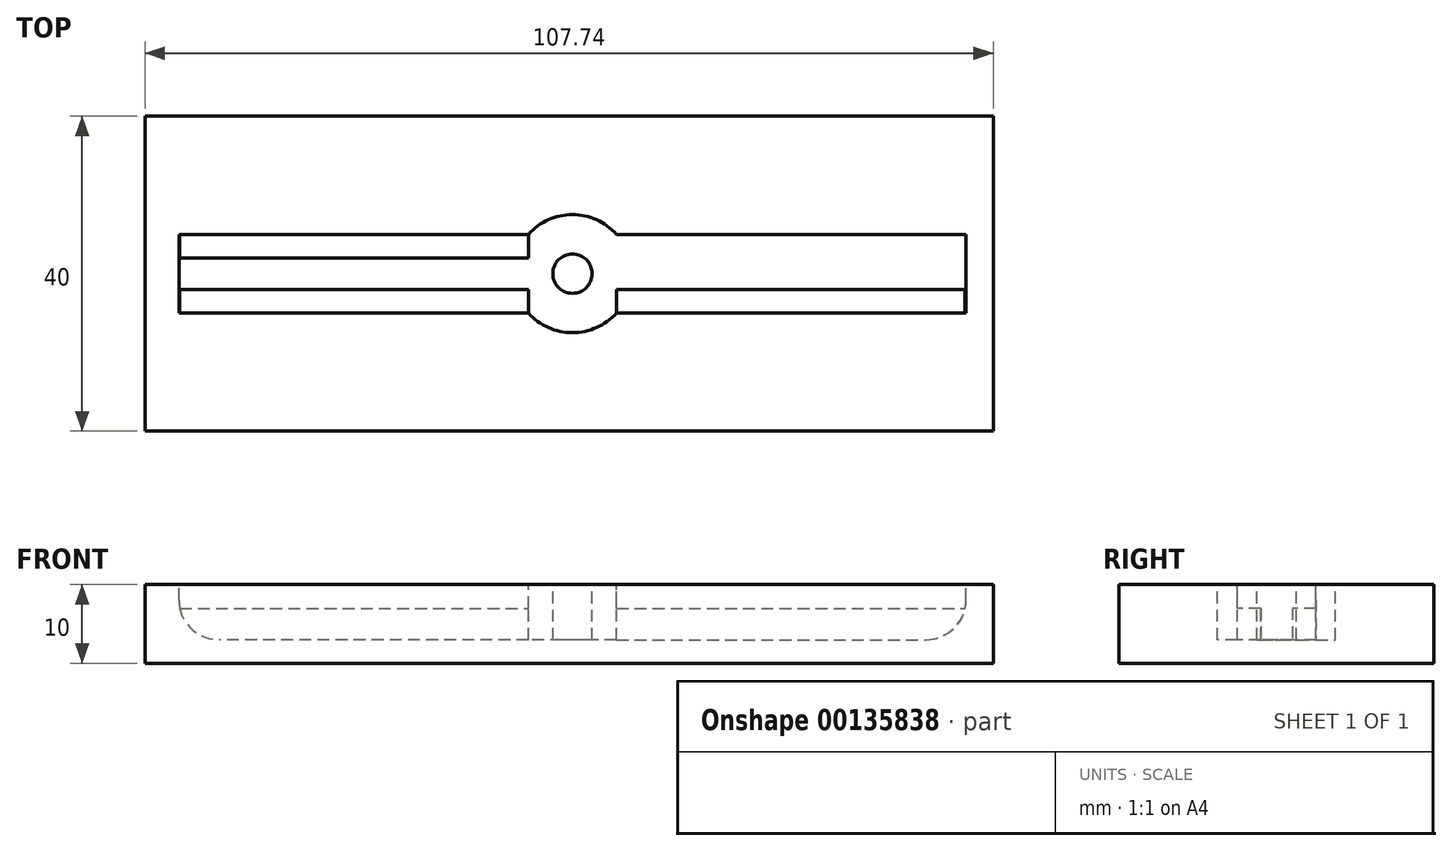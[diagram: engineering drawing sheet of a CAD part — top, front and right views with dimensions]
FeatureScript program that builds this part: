
annotation { "Feature Type Name" : "Feature", "Feature Type Description" : "" }
export const myFeature = defineFeature(function(context is Context, id is Id, definition is map)
    precondition{}
    {
        {
            var Q0;
            Q0=qCreatedBy(makeId("Top.planeOp"),FACE);
            var sketch = newSketch(context, id + "F0", { "sketchPlane" : qUnion([Q0])});
            skLineSegment(sketch, "E0.bottom", {"start": v(-102.53, -28.85) * mm, "end": v(47.47, -28.85) * mm});
            skLineSegment(sketch, "E0.top", {"start": v(-102.53, -68.85) * mm, "end": v(47.47, -68.85) * mm});
            skLineSegment(sketch, "E0.left", {"start": v(-102.53, -28.85) * mm, "end": v(-102.53, -68.85) * mm});
            skLineSegment(sketch, "E0.right", {"start": v(47.47, -28.85) * mm, "end": v(47.47, -68.85) * mm});
            skSolve(sketch);
        }
        {
            var Q0;
            Q0=makeQuery(id+"F0.imprint","IMPRINT",FACE,{"disambiguationData":[TD([[makeQuery(id+"F0.imprint","IMPRINT",EDGE,{"derivedFrom":sQuery(id+"F0.wireOp",EDGE,"E0.bottom")}),-1.0]])]});
            extrude(context, id + "F1", {"entities" : qUnion([Q0]), "depth" : 10 * mm});
        }
        {
            var Q0;
            Q0=makeQuery(id+"F1.opExtrude","CAP_FACE",FACE,{"disambiguationData":[OSD([sQuery(id+"F0.wireOp",EDGE,"E0.bottom"),sQuery(id+"F0.wireOp",EDGE,"E0.top"),sQuery(id+"F0.wireOp",EDGE,"E0.left"),sQuery(id+"F0.wireOp",EDGE,"E0.right")])],"isStart":false});
            var sketch = newSketch(context, id + "F2", { "sketchPlane" : qUnion([Q0])});
            skLineSegment(sketch, "E1", {"start": v(-102.53, -48.85) * mm, "end": v(-77.53, -48.85) * mm});
            skLineSegment(sketch, "E2", {"start": v(-27.53, -48.85) * mm, "end": v(-30.03, -48.85) * mm});
            skLineSegment(sketch, "E3", {"start": v(-30.03, -48.85) * mm, "end": v(-27.53, -48.85) * mm});
            skLineSegment(sketch, "E4", {"start": v(-27.53, -48.85) * mm, "end": v(-25.03, -48.85) * mm});
            skLineSegment(sketch, "E5", {"start": v(22.47, -48.85) * mm, "end": v(22.47, -43.85) * mm});
            skLineSegment(sketch, "E6", {"start": v(22.47, -43.85) * mm, "end": v(-21.94, -43.85) * mm});
            skLineSegment(sketch, "E7", {"start": v(-77.53, -43.85) * mm, "end": v(-77.53, -53.85) * mm});
            skLineSegment(sketch, "E8", {"start": v(-77.53, -53.85) * mm, "end": v(-33.12, -53.85) * mm});
            skLineSegment(sketch, "E9", {"start": v(22.47, -53.85) * mm, "end": v(22.47, -48.85) * mm});
            skCircle(sketch, "E10", {"center": v(-27.53, -48.85) * mm, "radius": 2.5 * mm});
            skArc(sketch, "E11", {"start": v(-21.94, -43.85) * mm, "mid": v(-27.53, -41.35) * mm, "end": v(-33.12, -43.85) * mm});
            skArc(sketch, "E12.trimOffspring", {"start": v(-33.12, -53.85) * mm, "mid": v(-27.53, -56.35) * mm, "end": v(-21.94, -53.85) * mm});
            skPoint(sketch, "E13.orphan", {"position": v(-77.53, -48.85) * mm});
            skLineSegment(sketch, "E14.trimOffspring", {"start": v(-30.03, -48.85) * mm, "end": v(-25.03, -48.85) * mm});
            skLineSegment(sketch, "E15.trimOffspring", {"start": v(22.47, -48.85) * mm, "end": v(47.47, -48.85) * mm});
            skLineSegment(sketch, "E16.trimOffspring", {"start": v(-33.12, -43.85) * mm, "end": v(-77.53, -43.85) * mm});
            skLineSegment(sketch, "E17.trimOffspring", {"start": v(-21.94, -53.85) * mm, "end": v(22.47, -53.85) * mm});
            skSolve(sketch);
        }
        {
            var Q0;
            Q0=makeQuery(id+"F2.imprint","IMPRINT",FACE,{"disambiguationData":[TD([[makeQuery(id+"F2.imprint","IMPRINT",EDGE,{"derivedFrom":sQuery(id+"F2.wireOp",EDGE,"E5")}),1.0]])]});
            extrude(context, id + "F3", {"entities" : qUnion([Q0]), "operationType" : NewBodyOperationType.REMOVE, "oppositeDirection" : true, "depth" : 7 * mm});
        }
        {
            var Q0;
            Q0=makeQuery(id+"F3.boolean.opBoolean","COPY",FACE,{"derivedFrom":makeQuery(id+"F3.opExtrude","CAP_FACE",FACE,{"disambiguationData":[OSD([sQuery(id+"F2.wireOp",EDGE,"E5"),sQuery(id+"F2.wireOp",EDGE,"E6"),sQuery(id+"F2.wireOp",EDGE,"E7"),sQuery(id+"F2.wireOp",EDGE,"E8"),sQuery(id+"F2.wireOp",EDGE,"E9"),sQuery(id+"F2.wireOp",EDGE,"E10"),sQuery(id+"F2.wireOp",EDGE,"E11"),sQuery(id+"F2.wireOp",EDGE,"E12.trimOffspring"),sQuery(id+"F2.wireOp",EDGE,"E16.trimOffspring"),sQuery(id+"F2.wireOp",EDGE,"E17.trimOffspring")])],"isStart":false})});
            var sketch = newSketch(context, id + "F4", { "sketchPlane" : qUnion([Q0])});
            skLineSegment(sketch, "E18.0", {"start": v(-77.53, -43.85) * mm, "end": v(-77.53, -53.85) * mm});
            skLineSegment(sketch, "E19.0", {"start": v(-33.12, -43.85) * mm, "end": v(-77.53, -43.85) * mm});
            skLineSegment(sketch, "E20.0", {"start": v(-77.53, -53.85) * mm, "end": v(-33.12, -53.85) * mm});
            skLineSegment(sketch, "E21.0", {"start": v(-21.94, -53.85) * mm, "end": v(22.47, -53.85) * mm});
            skLineSegment(sketch, "E22.0", {"start": v(22.47, -53.85) * mm, "end": v(22.47, -43.85) * mm});
            skLineSegment(sketch, "E23.0", {"start": v(-33.12, -46.85) * mm, "end": v(-77.53, -46.85) * mm});
            skLineSegment(sketch, "E24.0", {"start": v(-77.53, -50.85) * mm, "end": v(-33.12, -50.85) * mm});
            skPoint(sketch, "E25.0.end.orphan", {"position": v(-21.94, -43.85) * mm});
            skLineSegment(sketch, "E26.0", {"start": v(22.47, -43.85) * mm, "end": v(-21.94, -43.85) * mm});
            skLineSegment(sketch, "E27", {"start": v(-21.94, -43.85) * mm, "end": v(22.47, -43.85) * mm});
            skLineSegment(sketch, "E28.0", {"start": v(-21.94, -46.85) * mm, "end": v(22.47, -46.85) * mm});
            skLineSegment(sketch, "E29.0", {"start": v(-21.94, -50.85) * mm, "end": v(22.47, -50.85) * mm});
            skLineSegment(sketch, "E30", {"start": v(-21.94, -43.85) * mm, "end": v(-21.94, -53.85) * mm});
            skLineSegment(sketch, "E31", {"start": v(-33.12, -43.85) * mm, "end": v(-33.12, -53.85) * mm});
            skSolve(sketch);
        }
        {
            var Q0;
            {var subQ0=sQuery(id+"F4.wireOp",EDGE,"E19.0");Q0=makeQuery(id+"F4.imprint","IMPRINT",FACE,{"disambiguationData":[TD([[makeQuery(id+"F4.imprint","IMPRINT",EDGE,{"derivedFrom":subQ0}),1.0]])]});}
            var Q1;
            {var subQ0=sQuery(id+"F4.wireOp",EDGE,"E20.0");Q1=makeQuery(id+"F4.imprint","IMPRINT",FACE,{"disambiguationData":[TD([[makeQuery(id+"F4.imprint","IMPRINT",EDGE,{"derivedFrom":subQ0}),1.0]])]});}
            var Q2;
            {var subQ0=sQuery(id+"F4.wireOp",EDGE,"E21.0");Q2=makeQuery(id+"F4.imprint","IMPRINT",FACE,{"disambiguationData":[TD([[makeQuery(id+"F4.imprint","IMPRINT",EDGE,{"derivedFrom":subQ0}),1.0]])]});}
            var Q3;
            {var subQ0=sQuery(id+"F4.wireOp",EDGE,"E27");Q3=makeQuery(id+"F4.imprint","IMPRINT",FACE,{"disambiguationData":[TD([[makeQuery(id+"F4.imprint","IMPRINT",EDGE,{"derivedFrom":subQ0}),1.0]])]});}
            extrude(context, id + "F5", {"entities" : qUnion([Q0, Q1, Q2, Q3]), "operationType" : NewBodyOperationType.ADD, "depth" : 4 * mm});
        }
        {
            var Q0;
            Q0=makeQuery(id+"F3.boolean.opBoolean","COPY",EDGE,{"derivedFrom":makeQuery(id+"F3.opExtrude","CAP_EDGE",EDGE,{"disambiguationData":[OSD([sQuery(id+"F2.wireOp",EDGE,"E7")])],"isStart":false})});
            var Q1;
            Q1=makeQuery(id+"F3.boolean.opBoolean","COPY",EDGE,{"derivedFrom":makeQuery(id+"F3.opExtrude","CAP_EDGE",EDGE,{"disambiguationData":[OSD([sQuery(id+"F2.wireOp",EDGE,"E5"),sQuery(id+"F2.wireOp",EDGE,"E9")])],"isStart":false})});
            fillet(context, id + "F6", {"entities" : qUnion([Q0, Q1]), "radius" : 5.08 * mm, "tangentPropagation" : true, "allowEdgeOverflow" : false});
        }
        {
            var Q0;
            {var subQ0=sQuery(id+"F0.wireOp",EDGE,"E0.bottom");var subQ1=sQuery(id+"F0.wireOp",EDGE,"E0.left");var subQ2=sQuery(id+"F0.wireOp",EDGE,"E0.top");var subQ3=sQuery(id+"F0.wireOp",EDGE,"E0.right");Q0=makeQuery(id+"F3.boolean.opBoolean","SPLIT",FACE,{"disambiguationData":[TD([makeQuery(id+"F1.opExtrude","SWEPT_FACE",FACE,{"disambiguationData":[OSD([subQ0])]})])],"derivedFrom":makeQuery(id+"F1.opExtrude","CAP_FACE",FACE,{"disambiguationData":[OSD([subQ0,subQ2,subQ1,subQ3])],"isStart":false})});}
            var sketch = newSketch(context, id + "F7", { "sketchPlane" : qUnion([Q0])});
            skLineSegment(sketch, "E32.0", {"start": v(-102.53, -28.85) * mm, "end": v(47.47, -28.85) * mm});
            skLineSegment(sketch, "E33.0", {"start": v(-102.53, -28.85) * mm, "end": v(-102.53, -68.85) * mm});
            skLineSegment(sketch, "E34.0", {"start": v(-102.53, -68.85) * mm, "end": v(47.47, -68.85) * mm});
            skLineSegment(sketch, "E35.0", {"start": v(47.47, -28.85) * mm, "end": v(47.47, -68.85) * mm});
            skLineSegment(sketch, "E36", {"start": v(-102.53, -28.85) * mm, "end": v(-77.53, -28.85) * mm});
            skLineSegment(sketch, "E37", {"start": v(-77.53, -28.85) * mm, "end": v(-81.82, -28.85) * mm});
            skLineSegment(sketch, "E38", {"start": v(-81.82, -28.85) * mm, "end": v(-81.82, -68.85) * mm});
            skLineSegment(sketch, "E39", {"start": v(-81.82, -68.85) * mm, "end": v(47.47, -68.85) * mm});
            skLineSegment(sketch, "E40", {"start": v(47.47, -28.85) * mm, "end": v(22.47, -28.85) * mm});
            skLineSegment(sketch, "E41", {"start": v(22.47, -28.85) * mm, "end": v(25.92, -28.85) * mm});
            skLineSegment(sketch, "E42", {"start": v(25.92, -28.85) * mm, "end": v(25.92, -68.85) * mm});
            skLineSegment(sketch, "E43", {"start": v(25.92, -68.85) * mm, "end": v(47.47, -68.85) * mm});
            skSolve(sketch);
        }
        {
            var Q0;
            Q0=makeQuery(id+"F7.imprint","IMPRINT",FACE,{"disambiguationData":[TD([[makeQuery(id+"F7.imprint","IMPRINT",EDGE,{"derivedFrom":sQuery(id+"F7.wireOp",EDGE,"E33.0")}),1.0]])]});
            var Q1;
            Q1=makeQuery(id+"F7.imprint","IMPRINT",FACE,{"disambiguationData":[TD([[makeQuery(id+"F7.imprint","IMPRINT",EDGE,{"derivedFrom":sQuery(id+"F7.wireOp",EDGE,"E35.0")}),-1.0]])]});
            extrude(context, id + "F8", {"entities" : qUnion([Q0, Q1]), "operationType" : NewBodyOperationType.REMOVE, "oppositeDirection" : true, "depth" : 25.4 * mm});
        }
    });
